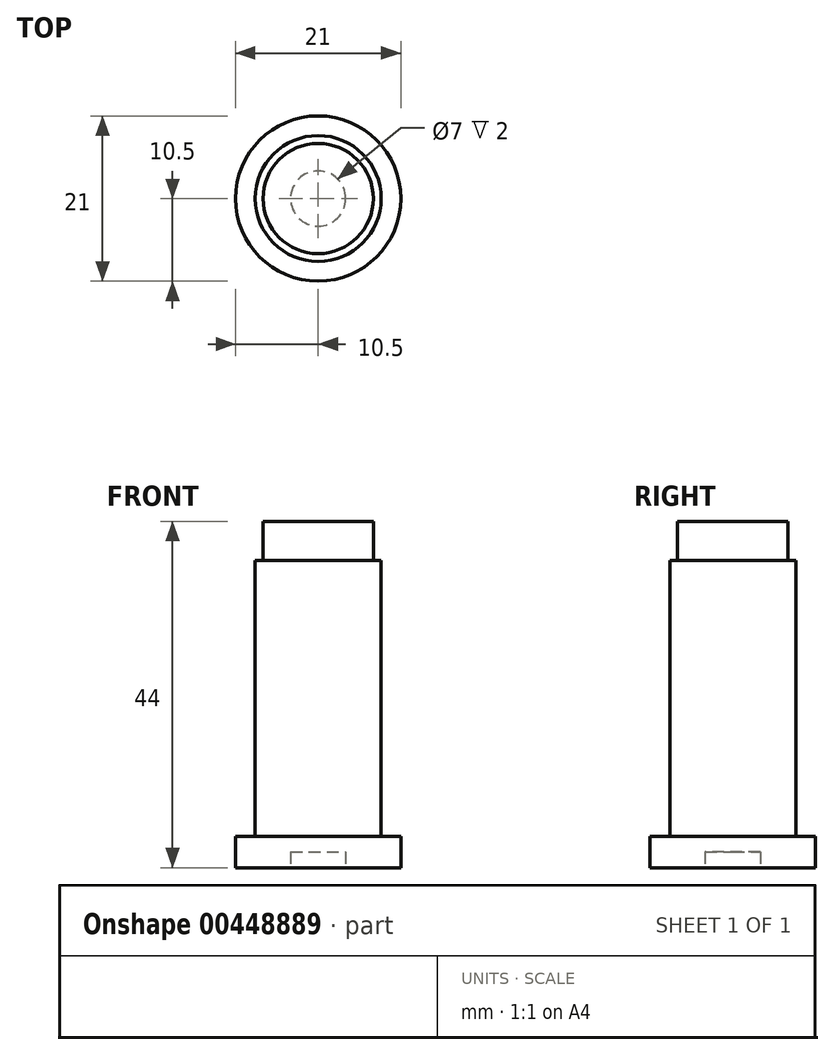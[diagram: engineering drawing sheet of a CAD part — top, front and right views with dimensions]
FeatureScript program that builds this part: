
annotation { "Feature Type Name" : "Feature", "Feature Type Description" : "" }
export const myFeature = defineFeature(function(context is Context, id is Id, definition is map)
    precondition{}
    {
        {
            var Q0;
            Q0=qCreatedBy(makeId("Top.planeOp"),FACE);
            var sketch = newSketch(context, id + "F0", { "sketchPlane" : qUnion([Q0])});
            skCircle(sketch, "E0", {"center": v(0, 0) * mm, "radius": 10.5 * mm});
            skSolve(sketch);
        }
        {
            var Q0;
            Q0=qSketchRegion(id+"F0",true);
            extrude(context, id + "F1", {"entities" : qUnion([Q0]), "depth" : 4 * mm});
        }
        {
            var Q0;
            Q0=qCreatedBy(makeId("Top.planeOp"),FACE);
            var sketch = newSketch(context, id + "F2", { "sketchPlane" : qUnion([Q0])});
            skCircle(sketch, "E1", {"center": v(0, 0) * mm, "radius": 8 * mm});
            skSolve(sketch);
        }
        {
            var Q0;
            Q0=qSketchRegion(id+"F2",true);
            extrude(context, id + "F3", {"entities" : qUnion([Q0]), "operationType" : NewBodyOperationType.ADD, "depth" : 39 * mm});
        }
        {
            var Q0;
            Q0=qCreatedBy(makeId("Right.planeOp"),FACE);
            var sketch = newSketch(context, id + "F4", { "sketchPlane" : qUnion([Q0])});
            skLineSegment(sketch, "E2", {"start": v(0, 44) * mm, "end": v(0, 39) * mm});
            skLineSegment(sketch, "E3", {"start": v(0, 39) * mm, "end": v(7, 39) * mm});
            skLineSegment(sketch, "E4", {"start": v(7, 39) * mm, "end": v(7, 44) * mm});
            skLineSegment(sketch, "E5", {"start": v(7, 44) * mm, "end": v(0, 44) * mm});
            skSolve(sketch);
        }
        {
            var Q0;
            Q0=makeQuery(id+"F4.imprint","IMPRINT",FACE,{"disambiguationData":[TD([[makeQuery(id+"F4.imprint","IMPRINT",EDGE,{"derivedFrom":sQuery(id+"F4.wireOp",EDGE,"E2")}),1.0]])]});
            var Q1;
            Q1=sQuery(id+"F4.wireOp",EDGE,"E2");
            revolve(context, id + "F5", {"operationType" : NewBodyOperationType.ADD, "entities" : qUnion([Q0]), "axis" : qUnion([Q1]), "revolveType" : RevolveType.FULL});
        }
        {
            var Q0;
            Q0=makeQuery(id+"F1.opExtrude","CAP_FACE",FACE,{"disambiguationData":[OSD([sQuery(id+"F0.wireOp",EDGE,"E0")])],"isStart":true});
            var sketch = newSketch(context, id + "F6", { "sketchPlane" : qUnion([Q0])});
            skCircle(sketch, "E6", {"center": v(0, 0) * mm, "radius": 3.5 * mm});
            skSolve(sketch);
        }
        {
            var Q0;
            Q0=qSketchRegion(id+"F6",true);
            extrude(context, id + "F7", {"entities" : qUnion([Q0]), "operationType" : NewBodyOperationType.REMOVE, "oppositeDirection" : true, "depth" : 2 * mm});
        }
    });
